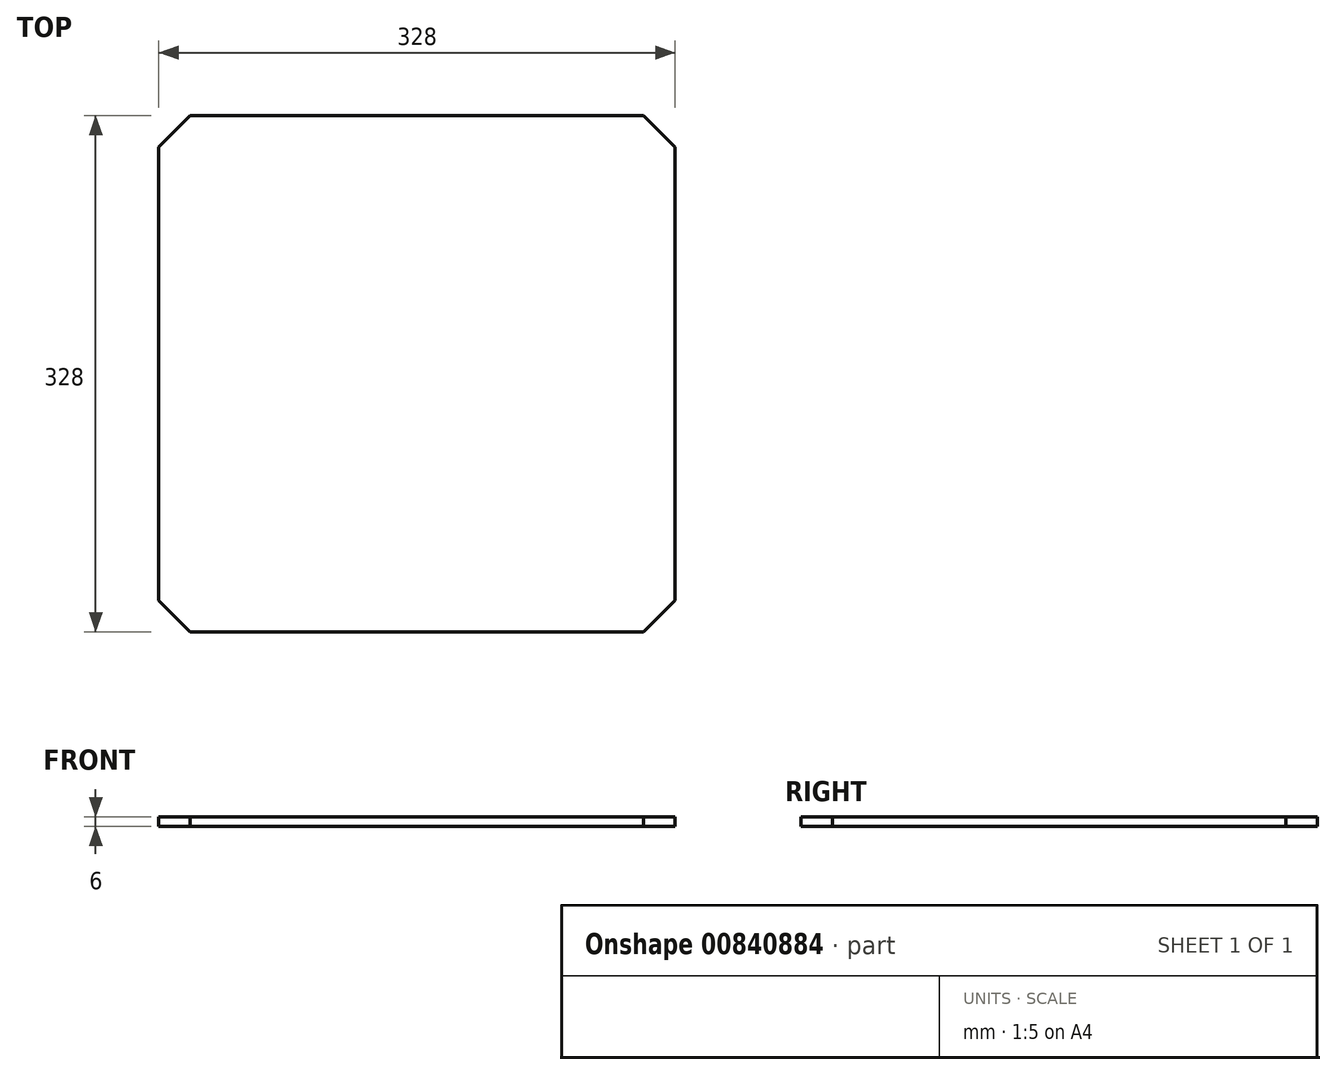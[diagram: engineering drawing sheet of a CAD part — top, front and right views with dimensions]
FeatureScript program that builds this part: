
annotation { "Feature Type Name" : "Feature", "Feature Type Description" : "" }
export const myFeature = defineFeature(function(context is Context, id is Id, definition is map)
    precondition{}
    {
        {
            var Q0;
            Q0=qCreatedBy(makeId("Top.planeOp"),FACE);
            var sketch = newSketch(context, id + "F0", { "sketchPlane" : qUnion([Q0])});
            skLineSegment(sketch, "E0.bottom", {"start": v(0, 0) * mm, "end": v(328, 0) * mm});
            skLineSegment(sketch, "E0.top", {"start": v(0, 328) * mm, "end": v(328, 328) * mm});
            skLineSegment(sketch, "E0.left", {"start": v(0, 0) * mm, "end": v(0, 328) * mm});
            skLineSegment(sketch, "E0.right", {"start": v(328, 0) * mm, "end": v(328, 328) * mm});
            skSolve(sketch);
        }
        {
            var Q0;
            Q0=qSketchRegion(id+"F0",true);
            extrude(context, id + "F1", {"entities" : qUnion([Q0]), "depth" : 6 * mm, "offsetDistance" : 25 * mm});
        }
        {
            var Q0;
            Q0=makeQuery(id+"F1.opExtrude","SWEPT_EDGE",EDGE,{"disambiguationData":[OSD([sQuery(id+"F0.wireOp",EDGE,"E0.top"),sQuery(id+"F0.wireOp",EDGE,"E0.right")])]});
            var Q1;
            Q1=makeQuery(id+"F1.opExtrude","SWEPT_EDGE",EDGE,{"disambiguationData":[OSD([sQuery(id+"F0.wireOp",EDGE,"E0.top"),sQuery(id+"F0.wireOp",EDGE,"E0.left")])]});
            var Q2;
            Q2=makeQuery(id+"F1.opExtrude","SWEPT_EDGE",EDGE,{"disambiguationData":[OSD([sQuery(id+"F0.wireOp",EDGE,"E0.bottom"),sQuery(id+"F0.wireOp",EDGE,"E0.left")])]});
            var Q3;
            Q3=makeQuery(id+"F1.opExtrude","SWEPT_EDGE",EDGE,{"disambiguationData":[OSD([sQuery(id+"F0.wireOp",EDGE,"E0.bottom"),sQuery(id+"F0.wireOp",EDGE,"E0.right")])]});
            chamfer(context, id + "F2", {"entities" : qUnion([Q0, Q1, Q2, Q3]), "width" : 20 * mm, "tangentPropagation" : true});
        }
    });
